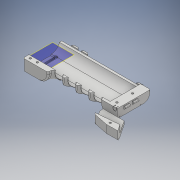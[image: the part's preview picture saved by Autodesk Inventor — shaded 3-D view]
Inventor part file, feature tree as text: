
AUTODESK INVENTOR PART (.ipt)
format: ipt  version: 2018 (Build 220112000, 112)  size: 7,383,552 bytes
history: native  units: mm
features: other x11, projected_geometry x5, extrude x2, sketch x2
ambient origin geometry x8: Origin, YZ Plane, XZ Plane, XY Plane, X Axis, Y Axis, Z Axis, Center Point
bodies: Body1 (feature_tree)
feature tree (20):
  other  "undercover_modified.ipt"
  other  "undercover1.ipt"
  other  "結合1"
  extrude  "押し出し1"  Depth=10.0mm
  extrude  "押し出し2"  Depth=10.0mm
  other  "ソリッド1::undercover_modified.ipt"
  other  "TaggingFeature1"
  other  "作業平面1"
  other  "ソリッド1::undercover1.ipt"
  other  "TaggingFeature2"
  other  "作業平面1_1"
  sketch  "スケッチ1"
  sketch  "スケッチ2"
  projected_geometry  "投影ループ1"
  projected_geometry  "投影ループ2"
  projected_geometry  "投影ループ3"
  projected_geometry  "投影ループ4"
  projected_geometry  "投影ループ5"
  other  "ソリッド1"
  other  "ソリッド2"
